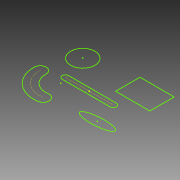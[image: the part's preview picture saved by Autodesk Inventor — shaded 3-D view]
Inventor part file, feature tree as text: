
AUTODESK INVENTOR PART (.ipt)
format: ipt  version: 2015 (Build 190159000, 159)  size: 64,000 bytes
history: native  units: mm
features: sketch x1
ambient origin geometry x8: Origin, YZ Plane, XZ Plane, XY Plane, X Axis, Y Axis, Z Axis, Center Point
feature tree (1):
  sketch  "Skizze1"
